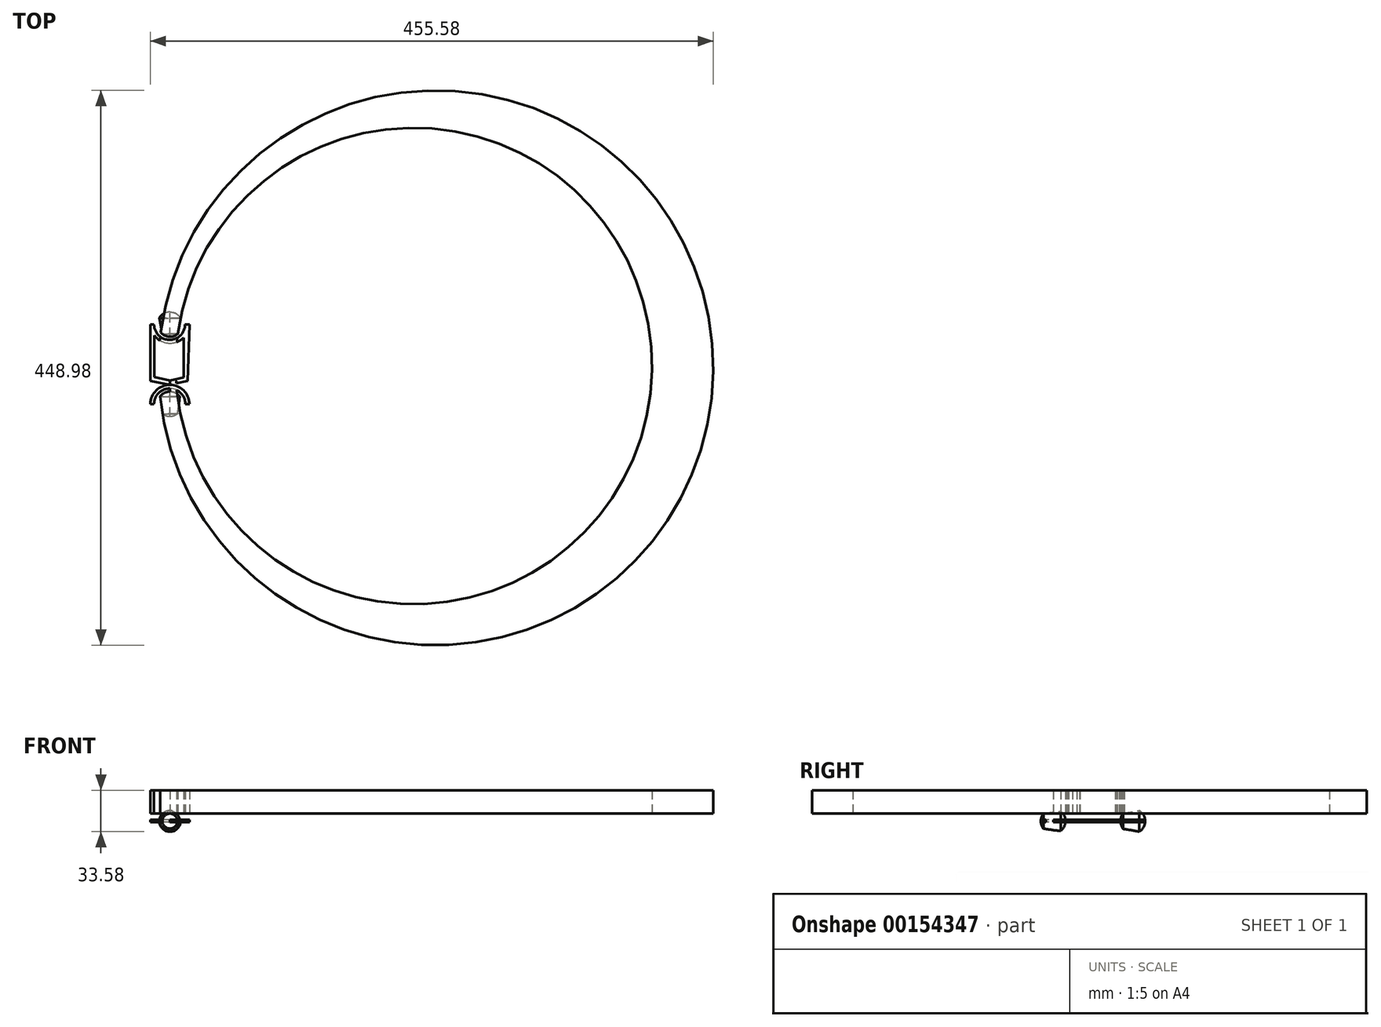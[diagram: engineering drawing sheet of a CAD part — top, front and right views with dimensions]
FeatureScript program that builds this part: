
annotation { "Feature Type Name" : "Feature", "Feature Type Description" : "" }
export const myFeature = defineFeature(function(context is Context, id is Id, definition is map)
    precondition{}
    {
        {
            var Q0;
            Q0=qCreatedBy(makeId("Top.planeOp"),FACE);
            var sketch = newSketch(context, id + "F0", { "sketchPlane" : qUnion([Q0])});
            skCircle(sketch, "E0", {"center": v(0, -32.53) * mm, "radius": 10 * mm});
            skCircle(sketch, "E1", {"center": v(0, 31.92) * mm, "radius": 10 * mm});
            skArc(sketch, "E2", {"start": v(-12.83, 31.92) * mm, "mid": v(-0.3, 19.37) * mm, "end": v(12.23, 31.92) * mm});
            skArc(sketch, "E3", {"start": v(12.53, -32.53) * mm, "mid": v(-0.15, -19.96) * mm, "end": v(-12.83, -32.53) * mm});
            skArc(sketch, "E4", {"start": v(15.8, -32.53) * mm, "mid": v(0, -17) * mm, "end": v(-15.8, -32.53) * mm});
            skLineSegment(sketch, "E5", {"start": v(-15.8, -32.53) * mm, "end": v(-12.83, -32.53) * mm});
            skLineSegment(sketch, "E6", {"start": v(12.53, -32.53) * mm, "end": v(15.8, -32.53) * mm});
            skArc(sketch, "E7", {"start": v(-15.8, 31.92) * mm, "mid": v(0, 16.65) * mm, "end": v(15.8, 31.92) * mm});
            skLineSegment(sketch, "E8", {"start": v(-15.8, 31.92) * mm, "end": v(-12.83, 31.92) * mm});
            skLineSegment(sketch, "E9", {"start": v(12.23, 31.92) * mm, "end": v(15.8, 31.92) * mm});
            skLineSegment(sketch, "E10", {"start": v(0, -17) * mm, "end": v(-15.8, -14.02) * mm});
            skLineSegment(sketch, "E11", {"start": v(-15.8, -14.02) * mm, "end": v(-15.8, 31.92) * mm});
            skLineSegment(sketch, "E12", {"start": v(15.8, 31.92) * mm, "end": v(14.21, -14.02) * mm});
            skLineSegment(sketch, "E13", {"start": v(14.21, -14.02) * mm, "end": v(0, -17) * mm});
            skLineSegment(sketch, "E14", {"start": v(0, -13.42) * mm, "end": v(-12.53, -10.74) * mm});
            skLineSegment(sketch, "E15", {"start": v(-12.53, -10.74) * mm, "end": v(-12.53, 22.8) * mm});
            skLineSegment(sketch, "E16", {"start": v(0, -13.42) * mm, "end": v(11.04, -11.04) * mm});
            skLineSegment(sketch, "E17", {"start": v(11.04, -11.04) * mm, "end": v(11.04, 21.13) * mm});
            skLineSegment(sketch, "E18", {"start": v(0, -42.53) * mm, "end": v(0, 41.92) * mm});
            skArc(sketch, "E19", {"start": v(7.83, 33.2) * mm, "mid": v(4.63, 0.04) * mm, "end": v(7.2, -33.17) * mm});
            skCircle(sketch, "E20", {"center": v(197.43, -1.8) * mm, "radius": 192.8 * mm});
            skArc(sketch, "E21", {"start": v(-6.26, 33) * mm, "mid": v(-9.18, 0.27) * mm, "end": v(-7.29, -32.53) * mm});
            skPoint(sketch, "E21.startSnap0", {"position": v(-6.26, -12.08) * mm});
            skCircle(sketch, "E22", {"center": v(215.28, -3.23) * mm, "radius": 224.49 * mm});
            skSolve(sketch);
        }
        {
            var Q0;
            Q0=makeQuery(id+"F0.imprint","IMPRINT",FACE,{"disambiguationData":[TD([[makeQuery(id+"F0.imprint","IMPRINT",EDGE,{"derivedFrom":sQuery(id+"F0.wireOp",EDGE,"E3")}),-1.0]])]});
            var Q1;
            Q1=makeQuery(id+"F0.imprint","IMPRINT",FACE,{"disambiguationData":[TD([[makeQuery(id+"F0.imprint","IMPRINT",EDGE,{"derivedFrom":sQuery(id+"F0.wireOp",EDGE,"E10")}),-1.0]])]});
            var Q2;
            Q2=makeQuery(id+"F0.imprint","IMPRINT",FACE,{"disambiguationData":[TD([[makeQuery(id+"F0.imprint","IMPRINT",EDGE,{"derivedFrom":sQuery(id+"F0.wireOp",EDGE,"E2")}),-1.0]])]});
            var Q3;
            {var subQ3=sQuery(id+"F0.wireOp",EDGE,"E12");Q3=makeQuery(id+"F0.imprint","IMPRINT",FACE,{"disambiguationData":[TD([[makeQuery(id+"F0.imprint","IMPRINT",EDGE,{"derivedFrom":subQ3}),-1.0]])]});}
            var Q4;
            {var subQ1=sQuery(id+"F0.wireOp",EDGE,"E13");var subQ3=sQuery(id+"F0.wireOp",EDGE,"E20");var subQ4=makeQuery(id+"F0.imprint","INTERSECT",VERTEX,{"derivedFrom":[subQ1,subQ3]});Q4=makeQuery(id+"F0.imprint","IMPRINT",FACE,{"disambiguationData":[TD([[makeQuery(id+"F0.imprint","IMPRINT",EDGE,{"disambiguationData":[TD([[subQ4,1.0]])],"derivedFrom":subQ3}),-1.0]])]});}
            var Q5;
            {var subQ0=sQuery(id+"F0.wireOp",EDGE,"E9");Q5=makeQuery(id+"F0.imprint","IMPRINT",FACE,{"disambiguationData":[TD([[makeQuery(id+"F0.imprint","IMPRINT",EDGE,{"derivedFrom":subQ0}),-1.0]])]});}
            var Q6;
            {var subQ0=sQuery(id+"F0.wireOp",EDGE,"E8");Q6=makeQuery(id+"F0.imprint","IMPRINT",FACE,{"disambiguationData":[TD([[makeQuery(id+"F0.imprint","IMPRINT",EDGE,{"derivedFrom":subQ0}),-1.0]])]});}
            var Q7;
            {var subQ0=sQuery(id+"F0.wireOp",EDGE,"E11");Q7=makeQuery(id+"F0.imprint","IMPRINT",FACE,{"disambiguationData":[TD([[makeQuery(id+"F0.imprint","IMPRINT",EDGE,{"derivedFrom":subQ0}),-1.0]])]});}
            extrude(context, id + "F1", {"entities" : qUnion([Q0, Q1, Q2, Q3, Q4, Q5, Q6, Q7]), "depth" : 1 * mm, "hasSecondDirection" : true, "secondDirectionOppositeDirection" : true, "secondDirectionDepth" : 1 * mm});
        }
        {
            var Q0;
            {var subQ0=sQuery(id+"F0.wireOp",EDGE,"E18");var subQ1=sQuery(id+"F0.wireOp",EDGE,"E0");var subQ2=makeQuery(id+"F0.imprint","INTERSECT",VERTEX,{"disambiguationData":[OD(0.0)],"derivedFrom":[subQ1,subQ0]});Q0=makeQuery(id+"F0.imprint","IMPRINT",FACE,{"disambiguationData":[TD([[makeQuery(id+"F0.imprint","IMPRINT",EDGE,{"disambiguationData":[TD([[subQ2,1.0]])],"derivedFrom":subQ1}),1.0]])]});}
            var Q1;
            {var subQ0=sQuery(id+"F0.wireOp",EDGE,"E18");var subQ1=sQuery(id+"F0.wireOp",EDGE,"E1");var subQ2=makeQuery(id+"F0.imprint","INTERSECT",VERTEX,{"disambiguationData":[OD(0.0)],"derivedFrom":[subQ1,subQ0]});Q1=makeQuery(id+"F0.imprint","IMPRINT",FACE,{"disambiguationData":[TD([[makeQuery(id+"F0.imprint","IMPRINT",EDGE,{"disambiguationData":[TD([[subQ2,-1.0]])],"derivedFrom":subQ1}),1.0]])]});}
            var Q2;
            {var subQ0=sQuery(id+"F0.wireOp",EDGE,"E22");var subQ4=makeQuery(id+"F0.imprint","IMPRINT",VERTEX,{"disambiguationData":[OD(1.0)],"derivedFrom":subQ0});Q2=makeQuery(id+"F0.imprint","IMPRINT",FACE,{"disambiguationData":[TD([[makeQuery(id+"F0.imprint","IMPRINT",EDGE,{"disambiguationData":[TD([[subQ4,1.0]])],"derivedFrom":subQ0}),-1.0]])]});}
            var Q3;
            {var subQ0=sQuery(id+"F0.wireOp",EDGE,"E22");var subQ4=makeQuery(id+"F0.imprint","IMPRINT",VERTEX,{"disambiguationData":[OD(0.0)],"derivedFrom":subQ0});Q3=makeQuery(id+"F0.imprint","IMPRINT",FACE,{"disambiguationData":[TD([[makeQuery(id+"F0.imprint","IMPRINT",EDGE,{"disambiguationData":[TD([[subQ4,1.0]])],"derivedFrom":subQ0}),-1.0]])]});}
            var Q4;
            Q4=sQuery(id+"F0.wireOp",EDGE,"E18");
            revolve(context, id + "F2", {"entities" : qUnion([Q0, Q1, Q2, Q3]), "axis" : qUnion([Q4]), "revolveType" : RevolveType.FULL});
        }
        {
            var Q0;
            {var subQ0=sQuery(id+"F0.wireOp",EDGE,"E20");var subQ1=makeQuery(id+"F0.imprint","IMPRINT",VERTEX,{"disambiguationData":[OD(0.0)],"derivedFrom":subQ0});Q0=makeQuery(id+"F0.imprint","IMPRINT",FACE,{"disambiguationData":[TD([[makeQuery(id+"F0.imprint","IMPRINT",EDGE,{"disambiguationData":[TD([[subQ1,1.0]])],"derivedFrom":subQ0}),-1.0]])]});}
            var Q1;
            {var subQ4=sQuery(id+"F0.wireOp",EDGE,"E22");var subQ6=makeQuery(id+"F0.imprint","IMPRINT",VERTEX,{"disambiguationData":[OD(0.0)],"derivedFrom":subQ4});Q1=makeQuery(id+"F0.imprint","IMPRINT",FACE,{"disambiguationData":[TD([[makeQuery(id+"F0.imprint","IMPRINT",EDGE,{"disambiguationData":[TD([[subQ6,1.0]])],"derivedFrom":subQ4}),1.0]])]});}
            var Q2;
            {var subQ0=sQuery(id+"F0.wireOp",EDGE,"E22");var subQ1=sQuery(id+"F0.wireOp",EDGE,"E1");var subQ2=makeQuery(id+"F0.imprint","INTERSECT",VERTEX,{"disambiguationData":[OD(1.0)],"derivedFrom":[subQ1,subQ0]});Q2=makeQuery(id+"F0.imprint","IMPRINT",FACE,{"disambiguationData":[TD([[makeQuery(id+"F0.imprint","IMPRINT",EDGE,{"disambiguationData":[TD([[subQ2,-1.0]])],"derivedFrom":subQ1}),-1.0]])]});}
            var Q3;
            {var subQ0=sQuery(id+"F0.wireOp",EDGE,"E18");var subQ1=sQuery(id+"F0.wireOp",EDGE,"E1");var subQ2=makeQuery(id+"F0.imprint","INTERSECT",VERTEX,{"disambiguationData":[OD(1.0)],"derivedFrom":[subQ1,subQ0]});Q3=makeQuery(id+"F0.imprint","IMPRINT",FACE,{"disambiguationData":[TD([[makeQuery(id+"F0.imprint","IMPRINT",EDGE,{"disambiguationData":[TD([[subQ2,-1.0]])],"derivedFrom":subQ1}),-1.0]])]});}
            var Q4;
            {var subQ0=sQuery(id+"F0.wireOp",EDGE,"E18");var subQ1=sQuery(id+"F0.wireOp",EDGE,"E2");var subQ2=makeQuery(id+"F0.imprint","INTERSECT",VERTEX,{"derivedFrom":[subQ1,subQ0]});Q4=makeQuery(id+"F0.imprint","IMPRINT",FACE,{"disambiguationData":[TD([[makeQuery(id+"F0.imprint","IMPRINT",EDGE,{"disambiguationData":[TD([[subQ2,-1.0]])],"derivedFrom":subQ1}),-1.0]])]});}
            var Q5;
            {var subQ0=sQuery(id+"F0.wireOp",EDGE,"E22");var subQ1=sQuery(id+"F0.wireOp",EDGE,"E2");var subQ2=makeQuery(id+"F0.imprint","INTERSECT",VERTEX,{"derivedFrom":[subQ1,subQ0]});Q5=makeQuery(id+"F0.imprint","IMPRINT",FACE,{"disambiguationData":[TD([[makeQuery(id+"F0.imprint","IMPRINT",EDGE,{"disambiguationData":[TD([[subQ2,-1.0]])],"derivedFrom":subQ1}),-1.0]])]});}
            var Q6;
            {var subQ0=sQuery(id+"F0.wireOp",EDGE,"E22");var subQ1=sQuery(id+"F0.wireOp",EDGE,"E7");var subQ2=makeQuery(id+"F0.imprint","INTERSECT",VERTEX,{"derivedFrom":[subQ1,subQ0]});Q6=makeQuery(id+"F0.imprint","IMPRINT",FACE,{"disambiguationData":[TD([[makeQuery(id+"F0.imprint","IMPRINT",EDGE,{"disambiguationData":[TD([[subQ2,-1.0]])],"derivedFrom":subQ1}),-1.0]])]});}
            var Q7;
            {var subQ0=sQuery(id+"F0.wireOp",EDGE,"E18");var subQ1=sQuery(id+"F0.wireOp",EDGE,"E7");var subQ2=makeQuery(id+"F0.imprint","INTERSECT",VERTEX,{"derivedFrom":[subQ1,subQ0]});Q7=makeQuery(id+"F0.imprint","IMPRINT",FACE,{"disambiguationData":[TD([[makeQuery(id+"F0.imprint","IMPRINT",EDGE,{"disambiguationData":[TD([[subQ2,-1.0]])],"derivedFrom":subQ1}),-1.0]])]});}
            var Q8;
            {var subQ1=sQuery(id+"F0.wireOp",EDGE,"E10");var subQ3=sQuery(id+"F0.wireOp",EDGE,"E22");var subQ4=makeQuery(id+"F0.imprint","INTERSECT",VERTEX,{"derivedFrom":[subQ1,subQ3]});Q8=makeQuery(id+"F0.imprint","IMPRINT",FACE,{"disambiguationData":[TD([[makeQuery(id+"F0.imprint","IMPRINT",EDGE,{"disambiguationData":[TD([[subQ4,1.0]])],"derivedFrom":subQ3}),1.0]])]});}
            var Q9;
            {var subQ1=sQuery(id+"F0.wireOp",EDGE,"E13");var subQ3=sQuery(id+"F0.wireOp",EDGE,"E20");var subQ4=makeQuery(id+"F0.imprint","INTERSECT",VERTEX,{"derivedFrom":[subQ1,subQ3]});Q9=makeQuery(id+"F0.imprint","IMPRINT",FACE,{"disambiguationData":[TD([[makeQuery(id+"F0.imprint","IMPRINT",EDGE,{"disambiguationData":[TD([[subQ4,1.0]])],"derivedFrom":subQ3}),-1.0]])]});}
            var Q10;
            {var subQ1=sQuery(id+"F0.wireOp",EDGE,"E4");var subQ3=sQuery(id+"F0.wireOp",EDGE,"E20");var subQ4=makeQuery(id+"F0.imprint","INTERSECT",VERTEX,{"derivedFrom":[subQ1,subQ3]});Q10=makeQuery(id+"F0.imprint","IMPRINT",FACE,{"disambiguationData":[TD([[makeQuery(id+"F0.imprint","IMPRINT",EDGE,{"disambiguationData":[TD([[subQ4,1.0]])],"derivedFrom":subQ3}),-1.0]])]});}
            var Q11;
            {var subQ1=sQuery(id+"F0.wireOp",EDGE,"E4");var subQ3=sQuery(id+"F0.wireOp",EDGE,"E22");var subQ4=makeQuery(id+"F0.imprint","INTERSECT",VERTEX,{"derivedFrom":[subQ1,subQ3]});Q11=makeQuery(id+"F0.imprint","IMPRINT",FACE,{"disambiguationData":[TD([[makeQuery(id+"F0.imprint","IMPRINT",EDGE,{"disambiguationData":[TD([[subQ4,1.0]])],"derivedFrom":subQ3}),1.0]])]});}
            var Q12;
            {var subQ0=sQuery(id+"F0.wireOp",EDGE,"E22");var subQ1=sQuery(id+"F0.wireOp",EDGE,"E3");var subQ2=makeQuery(id+"F0.imprint","INTERSECT",VERTEX,{"derivedFrom":[subQ1,subQ0]});Q12=makeQuery(id+"F0.imprint","IMPRINT",FACE,{"disambiguationData":[TD([[makeQuery(id+"F0.imprint","IMPRINT",EDGE,{"disambiguationData":[TD([[subQ2,1.0]])],"derivedFrom":subQ1}),-1.0]])]});}
            var Q13;
            {var subQ0=sQuery(id+"F0.wireOp",EDGE,"E20");var subQ1=sQuery(id+"F0.wireOp",EDGE,"E3");var subQ2=makeQuery(id+"F0.imprint","INTERSECT",VERTEX,{"derivedFrom":[subQ1,subQ0]});Q13=makeQuery(id+"F0.imprint","IMPRINT",FACE,{"disambiguationData":[TD([[makeQuery(id+"F0.imprint","IMPRINT",EDGE,{"disambiguationData":[TD([[subQ2,-1.0]])],"derivedFrom":subQ1}),-1.0]])]});}
            var Q14;
            {var subQ0=sQuery(id+"F0.wireOp",EDGE,"E18");var subQ1=sQuery(id+"F0.wireOp",EDGE,"E0");var subQ2=makeQuery(id+"F0.imprint","INTERSECT",VERTEX,{"disambiguationData":[OD(1.0)],"derivedFrom":[subQ1,subQ0]});Q14=makeQuery(id+"F0.imprint","IMPRINT",FACE,{"disambiguationData":[TD([[makeQuery(id+"F0.imprint","IMPRINT",EDGE,{"disambiguationData":[TD([[subQ2,1.0]])],"derivedFrom":subQ1}),-1.0]])]});}
            var Q15;
            {var subQ0=sQuery(id+"F0.wireOp",EDGE,"E22");var subQ1=sQuery(id+"F0.wireOp",EDGE,"E0");var subQ2=makeQuery(id+"F0.imprint","INTERSECT",VERTEX,{"disambiguationData":[OD(0.0)],"derivedFrom":[subQ1,subQ0]});Q15=makeQuery(id+"F0.imprint","IMPRINT",FACE,{"disambiguationData":[TD([[makeQuery(id+"F0.imprint","IMPRINT",EDGE,{"disambiguationData":[TD([[subQ2,1.0]])],"derivedFrom":subQ1}),-1.0]])]});}
            var Q16;
            {var subQ0=sQuery(id+"F0.wireOp",EDGE,"E22");var subQ1=makeQuery(id+"F0.imprint","IMPRINT",VERTEX,{"disambiguationData":[OD(1.0)],"derivedFrom":subQ0});Q16=makeQuery(id+"F0.imprint","IMPRINT",FACE,{"disambiguationData":[TD([[makeQuery(id+"F0.imprint","IMPRINT",EDGE,{"disambiguationData":[TD([[subQ1,1.0]])],"derivedFrom":subQ0}),1.0]])]});}
            var Q17;
            {var subQ0=sQuery(id+"F0.wireOp",EDGE,"E20");var subQ1=makeQuery(id+"F0.imprint","IMPRINT",VERTEX,{"disambiguationData":[OD(1.0)],"derivedFrom":subQ0});Q17=makeQuery(id+"F0.imprint","IMPRINT",FACE,{"disambiguationData":[TD([[makeQuery(id+"F0.imprint","IMPRINT",EDGE,{"disambiguationData":[TD([[subQ1,1.0]])],"derivedFrom":subQ0}),-1.0]])]});}
            var Q18;
            {var subQ0=sQuery(id+"F0.wireOp",EDGE,"E18");var subQ7=sQuery(id+"F0.wireOp",EDGE,"E0");var subQ8=makeQuery(id+"F0.imprint","INTERSECT",VERTEX,{"disambiguationData":[OD(0.0)],"derivedFrom":[subQ7,subQ0]});Q18=makeQuery(id+"F0.imprint","IMPRINT",FACE,{"disambiguationData":[TD([[makeQuery(id+"F0.imprint","IMPRINT",EDGE,{"disambiguationData":[TD([[subQ8,1.0]])],"derivedFrom":subQ7}),-1.0]])]});}
            extrude(context, id + "F3", {"entities" : qUnion([Q0, Q1, Q2, Q3, Q4, Q5, Q6, Q7, Q8, Q9, Q10, Q11, Q12, Q13, Q14, Q15, Q16, Q17, Q18]), "depth" : 25 * mm, "hasSecondDirection" : true, "secondDirectionOppositeDirection" : false, "secondDirectionDepth" : 6.25 * mm});
        }
    });
